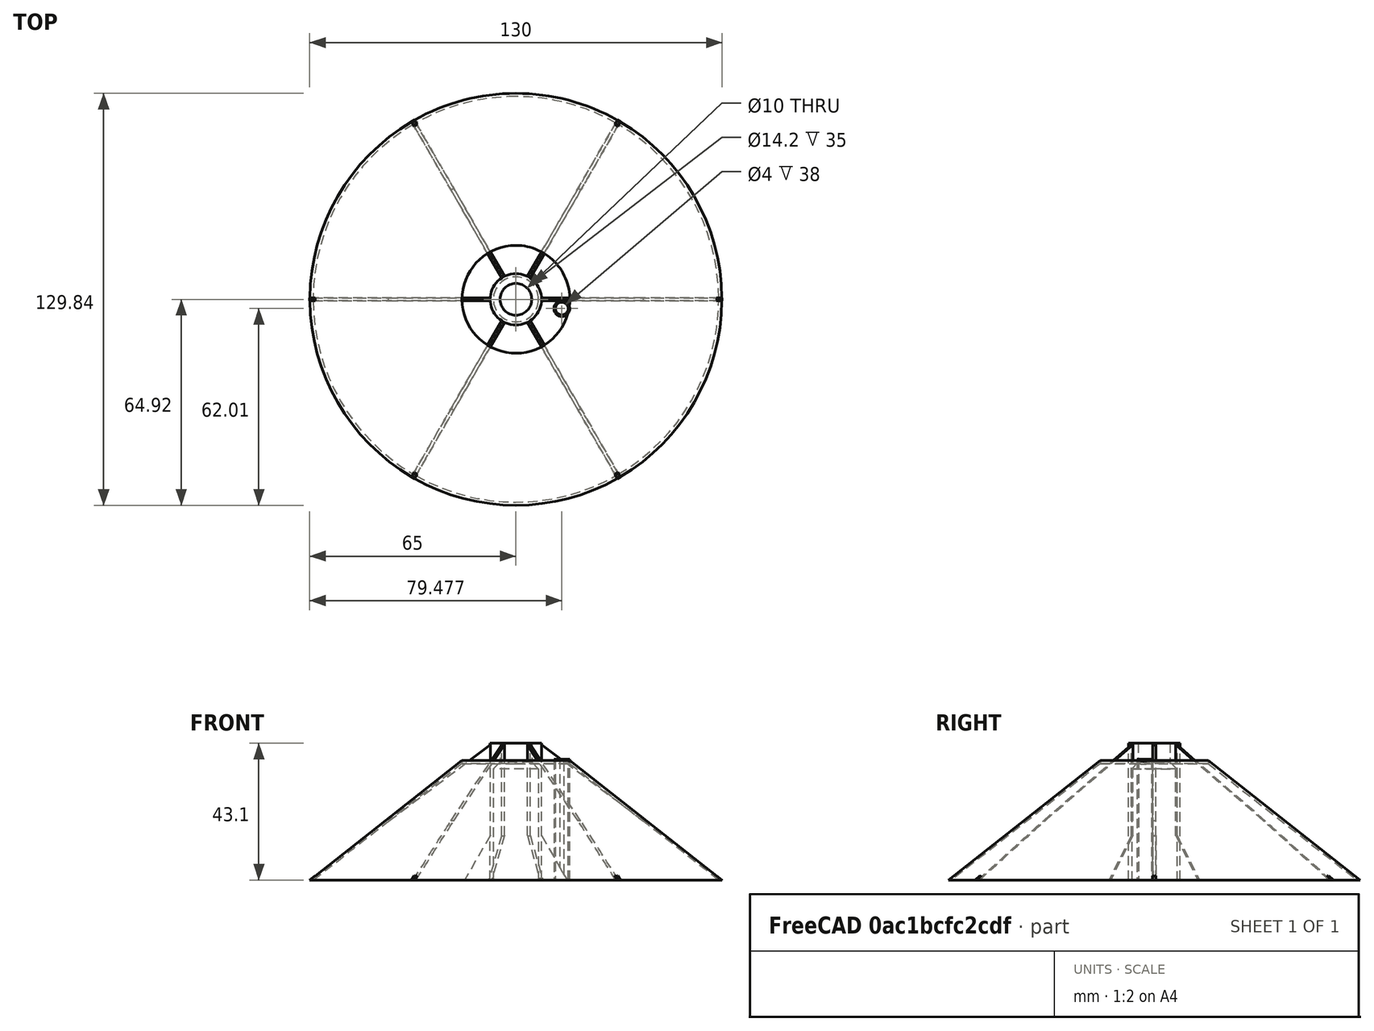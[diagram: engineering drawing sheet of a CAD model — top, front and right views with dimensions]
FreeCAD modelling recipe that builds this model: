
FCSTD DOCUMENT  (FreeCAD 0.20R29603 (Git))
Label: Ez3D-Mini-Saucerv3
License: All rights reserved
LicenseURL: http://en.wikipedia.org/wiki/All_rights_reserved
objects: Sketcher::SketchObject×4, PartDesign::Revolution×2, PartDesign::Pad×2, PartDesign::PolarPattern×1, PartDesign::Plane×1, Mesh::Feature×1, PartDesign::Body×1
note: 15 computed .brp shape members not serialized (recipe doc carries the construction recipe); baked Part::Feature solids carry a one-line shape summary decoded from their .brp

FEATURE [Sketcher::SketchObject] Sketch  label="Fin Can and Transition"
  FullyConstrained = true
  MapMode = 5
  Placement = pos=(0,0,0) rot=(1,0,0;1.5708rad)
  Support = -> [XZ_Plane]
  sketch-geometry (6):
    g0: LineSegment StartX=7.1 StartY=0 StartZ=0 EndX=8.1 EndY=0 EndZ=0
    g1: LineSegment StartX=8.1 StartY=0 StartZ=0 EndX=8.1 EndY=43.1 EndZ=0
    g2: LineSegment StartX=5 StartY=43.1 StartZ=0 EndX=5 EndY=37.1 EndZ=0
    g3: LineSegment StartX=5 StartY=37.1 StartZ=0 EndX=7.1 EndY=35 EndZ=0
    g4: LineSegment StartX=7.1 StartY=35 StartZ=0 EndX=7.1 EndY=0 EndZ=0
    g5: LineSegment StartX=5 StartY=43.1 StartZ=0 EndX=8.1 EndY=43.1 EndZ=0
  constraints (18):
    c: PointOnObject(g0,g-1)
    c: PointOnObject(g0,g-1)
    c: Coincident(g0,g1)
    c: Vertical(g1)
    c: Vertical(g2)
    c: Coincident(g2,g3)
    c: Coincident(g3,g4)
    c: Coincident(g4,g0)
    c: Vertical(g4)
    c: DistanceX(g0,g0) = 1
    c: DistanceX(g-1,g0) = 7.1
    c: DistanceY(g0,g3) = 35
    c: Angle(g3) = -0.785398
    c: DistanceX(g-1,g2) = 5
    c: DistanceY(g2,g2) = 6
    c: Horizontal(g2,g1)
    c: Coincident(g5,g2)
    c: Coincident(g5,g1)
FEATURE [PartDesign::Revolution] Revolution  label="Revolution for Fin Can"
  Angle = 360
  Axis = (0,-2e-16,1)
  Base = (0,0,0)
  Placement = pos=(0,0,0) rot=(1,0,0;1.5708rad)
  Profile = -> Sketch
  ReferenceAxis = -> Sketch [V_Axis]
  Reversed = true
FEATURE [Sketcher::SketchObject] Sketch001  label="Fin"
  FullyConstrained = true
  MapMode = 5
  Placement = pos=(0,0,0) rot=(1,0,0;1.5708rad)
  Support = -> [XZ_Plane]
  sketch-geometry (4):
    g0: LineSegment StartX=16.1603 StartY=0 StartZ=0 EndX=65 EndY=0 EndZ=0
    g1: LineSegment StartX=65 StartY=0 StartZ=0 EndX=7.5 EndY=43 EndZ=0
    g2: LineSegment StartX=7.5 StartY=43 StartZ=0 EndX=7.5 EndY=15 EndZ=0
    g3: LineSegment StartX=7.5 StartY=15 StartZ=0 EndX=16.1603 EndY=0 EndZ=0
  constraints (12):
    c: Horizontal(g0)
    c: Coincident(g1,g2)
    c: Vertical(g2)
    c: Coincident(g2,g3)
    c: Coincident(g0,g3)
    c: DistanceX(g-1,g1) = 7.5
    c: Angle(g3) = -1.0472
    c: PointOnObject(g0,g-1)
    c: DistanceY(g2,g2) = 28
    c: DistanceY(g0,g1) = 43
    c: Coincident(g1,g0)
    c: DistanceX(g-1,g0) = 65
FEATURE [PartDesign::Pad] Pad  label="Fin 2mm thick"
  BaseFeature = -> Revolution
  Direction = (0,-1,-2e-16)
  Length = 1
  Length2 = 100
  Midplane = true
  Placement = pos=(0,0,0) rot=(1,0,0;1.5708rad)
  Profile = -> Sketch001
  ReferenceAxis = -> Sketch001 [N_Axis]
  Type = 0
FEATURE [PartDesign::PolarPattern] PolarPattern  label="Add Multiple Fins"
  Angle = 360
  Axis = -> Z_Axis
  BaseFeature = -> Pad
  Occurrences = 6
  Originals = -> [Pad]
  Placement = pos=(0,0,0) rot=(1,0,0;1.5708rad)
FEATURE [Sketcher::SketchObject] Sketch002  label="Launch Lug 4mm ID 5mm OD"
  FullyConstrained = false
  MapMode = 5
  Support = -> [XY_Plane]
  sketch-geometry (2):
    g0: Circle CenterX=14.4768 CenterY=-2.91019 CenterZ=0 NormalX=0 NormalY=0 NormalZ=1 AngleXU=0 Radius=2.5
    g1: Circle CenterX=14.4768 CenterY=-2.91019 CenterZ=0 NormalX=0 NormalY=0 NormalZ=1 AngleXU=0 Radius=2
  constraints (3):
    c: Coincident(g1,g0)
    c: Diameter(g0) = 5
    c: Diameter(g1) = 4
FEATURE [PartDesign::Pad] Pad001  label="Launch Lug 62mm long"
  BaseFeature = -> PolarPattern
  Direction = (0,0,1)
  Length = 38
  Length2 = 100
  Placement = pos=(0,0,0) rot=(1,0,0;1.5708rad)
  Profile = -> Sketch002
  ReferenceAxis = -> Sketch002 [N_Axis]
  Type = 0
FEATURE [PartDesign::Plane] DatumPlane  label="DatumPlane for Recovery Harness Hole"
  Length = 103.416
  MapMode = 5
  Placement = pos=(0,0,0) rot=(1,0,0;3.14159rad)
  ResizeMode = 0
  Support = -> [Pad001]
  Width = 63.4164
FEATURE [Mesh::Feature] _3mmThread20x2_5_5mmTall  label="13mmThread20x2.5-5mmTall"
FEATURE [Sketcher::SketchObject] Sketch004  label="Saucer Body"
  FullyConstrained = false
  MapMode = 5
  Placement = pos=(0,0,0) rot=(0.57735,0.57735,0.57735;2.0944rad)
  Support = -> [YZ_Plane]
  sketch-geometry (4):
    g0: LineSegment StartX=17 StartY=36.6842 StartZ=0 EndX=63.9164 EndY=0 EndZ=0
    g1: LineSegment StartX=64.9164 StartY=0 StartZ=0 EndX=17 EndY=37.6842 EndZ=0
    g2: LineSegment StartX=63.9164 StartY=0 StartZ=0 EndX=64.9164 EndY=0 EndZ=0
    g3: LineSegment StartX=17 StartY=37.6842 StartZ=0 EndX=17 EndY=36.6842 EndZ=0
  constraints (10):
    c: PointOnObject(g0,g-1)
    c: PointOnObject(g1,g-1)
    c: Coincident(g2,g0)
    c: Coincident(g2,g1)
    c: DistanceX(g2,g2) = 1
    c: Coincident(g3,g1)
    c: Coincident(g3,g0)
    c: Vertical(g3)
    c: DistanceY(g3,g3) = 1
    c: DistanceX(g-1,g0) = 17
FEATURE [PartDesign::Revolution] Revolution001
  Angle = 360
  Axis = (-2e-16,3e-16,1)
  Base = (0,0,0)
  BaseFeature = -> Pad001
  Placement = pos=(0,0,0) rot=(1,0,0;1.5708rad)
  Profile = -> Sketch004
  ReferenceAxis = -> Sketch004 [V_Axis]
  Reversed = true
FEATURE [PartDesign::Body] Body
  Group = -> [Sketch,Revolution,Sketch001,Pad,PolarPattern,Sketch002,Pad001,DatumPlane,Sketch004,Revolution001]
  Origin = -> Origin
  Tip = -> Revolution001
